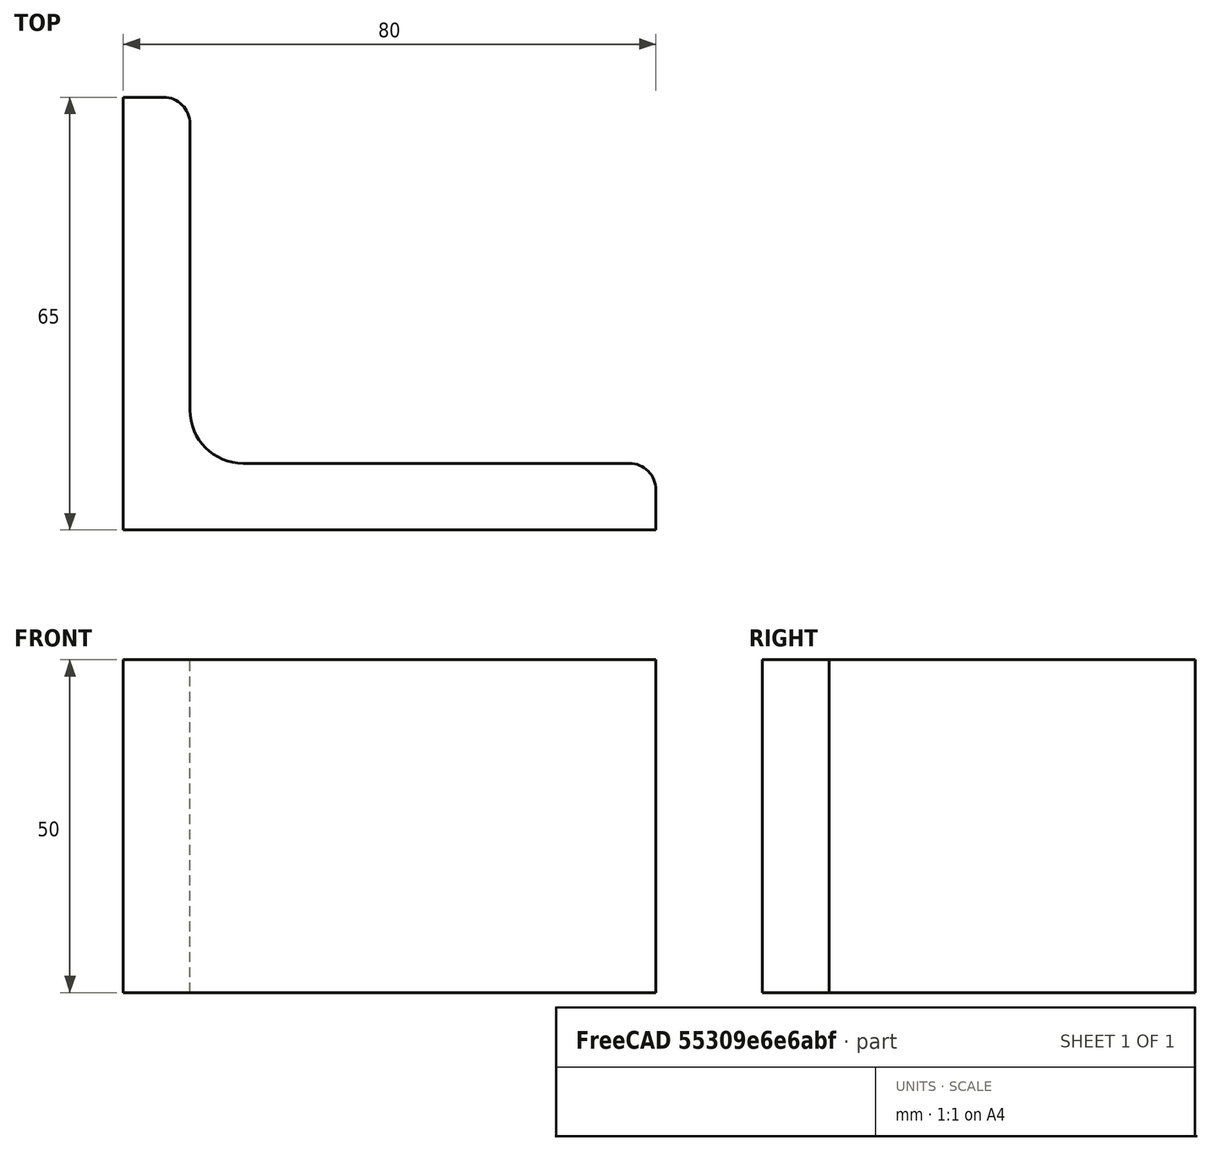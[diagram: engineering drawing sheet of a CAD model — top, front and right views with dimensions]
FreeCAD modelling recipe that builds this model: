
FCSTD DOCUMENT  (FreeCAD 0.15R4671 (Git))
Label: Angle Bar 80x65x10 EN10056 S235JR
License: All rights reserved
LicenseURL: http://en.wikipedia.org/wiki/All_rights_reserved
objects: Sketcher::SketchObject×1, Part::Extrusion×1
note: 2 computed .brp shape members not serialized (recipe doc carries the construction recipe); baked Part::Feature solids carry a one-line shape summary decoded from their .brp

FEATURE [Sketcher::SketchObject] Sketch
  sketch-geometry (9):
    g0: LineSegment StartX=0 StartY=0 StartZ=0 EndX=80 EndY=0 EndZ=0
    g1: LineSegment StartX=80 StartY=0 StartZ=0 EndX=80 EndY=6 EndZ=0
    g2: LineSegment StartX=76 StartY=10 StartZ=0 EndX=18 EndY=10 EndZ=0
    g3: LineSegment StartX=0 StartY=0 StartZ=0 EndX=0 EndY=65 EndZ=0
    g4: LineSegment StartX=0 StartY=65 StartZ=0 EndX=6 EndY=65 EndZ=0
    g5: LineSegment StartX=10 StartY=61 StartZ=0 EndX=10 EndY=18 EndZ=0
    g6: ArcOfCircle CenterX=18 CenterY=18 CenterZ=0 NormalX=0 NormalY=0 NormalZ=1 Radius=8 StartAngle=3.14159 EndAngle=4.71239
    g7: ArcOfCircle CenterX=6 CenterY=61 CenterZ=0 NormalX=0 NormalY=0 NormalZ=1 Radius=4 StartAngle=0 EndAngle=1.5708
    g8: ArcOfCircle CenterX=76 CenterY=6 CenterZ=0 NormalX=0 NormalY=0 NormalZ=1 Radius=4 StartAngle=0 EndAngle=1.5708
  constraints (23):
    c: Coincident(g0,g-1)
    c: Horizontal(g0)
    c: Coincident(g1,g0)
    c: Vertical(g1)
    c: Horizontal(g2)
    c: Coincident(g3,g-1)
    c: Vertical(g3)
    c: Coincident(g4,g3)
    c: Horizontal(g4)
    c: Vertical(g5)
    c: Tangent(g5,g6) = -1.5708
    c: Tangent(g2,g6) = 1.5708
    c: Tangent(g4,g7) = 1.5708
    c: Tangent(g5,g7) = 1.5708
    c: Tangent(g2,g8) = -1.5708
    c: Tangent(g1,g8) = -1.5708
    c: DistanceX(g0) = 80
    c: DistanceY(g3) = 65
    c: DistanceY(g0,g2) = 10
    c: DistanceX(g3,g5) = 10
    c: Radius(g6) = 8
    c: Radius(g8) = 4
    c: Radius(g7) = 4
FEATURE [Part::Extrusion] Extrude  label="Angle Bar 80x65x10 EN10056 S235JR"
  Base = -> Sketch
  Dir = (0,0,50)
  Solid = true
